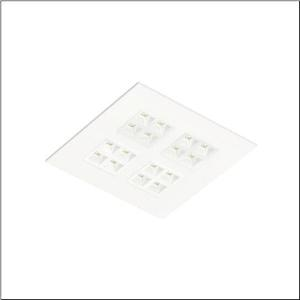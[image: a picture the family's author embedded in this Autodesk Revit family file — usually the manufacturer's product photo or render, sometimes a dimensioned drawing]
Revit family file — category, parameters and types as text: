
# Revit family: silica_31_square_51my6nms34wa
name_source: partatom
category: Lighting Fixtures
units: mm (PartAtom-declared; Revit-internal decimal feet)

## family parameters
Cut with Voids When Loaded = No
Host = Face
Light Source = No
Part Type = Normal
Room Calculation Point = No
Round Connector Dimension = Use Diameter
Shared = No

## types (1)
- --- (1 x LED, 6600 lm, 39 W, 3000K)
    Apparent Load = 39 VA
    CIE Flux Codes = 81 99 100 100 100
    Color Rendering = 80
    Color Temperature = 3000K
    Default Elevation = 1800 mm
    Description = Silica 31 Square, office luminaire, primary light control with lens, of PMMA, primary anti-glare with reflector, of PC, white, light emission: direct distribution, primary light characteristic: symmetric, installation type: lay-in mounting, LED, rated luminous flux: 4.580lm, luminous efficacy: 176lm/W, light colour: 830, colour temperature: 3000K, control gear: ON/OFF Multilumen, with terminal, 3-pole, mains connection: 220..240V, AC, 50/60Hz, rated input power: 26W, luminaire housing, of sheet steel, coated, traffic white (RAL 9016), module: M600, length: 595mm, width: 595mm, height: 43mm, protection rating (complete): IP20, insulation class (complete): insulation class II (safety insulation), certification: CE, impact resistance: IK03, permissible operating ambient temperature: -20..+35°C, standard: EN 50419, packaging unit: 1 piece
    Height = 0 mm  [stored 0 ft]
    Lamp = 1 x LED
    Lamp Light Flux = 6600 lm
    Lamp Power = 39 W
    Lamp count = 1
    Length = 595 mm
    Luminous efficacy = 169 lm/W
    Manufacturer = Siteco
    ModVariant = No
    Model = 51MY6NMS34WA
    Mounting Place = Ceiling
    Mounting Type = Recessed
    Number of Poles = 1
    OnlyDefault = Yes
    Power Factor = 1
    Product Name = Silica 31 Square
    Product group = office luminaire | ceiling recessed
    ProductGroupID = 400
    Protection Class = Protection class II
    Protection Degree = IP 20
    RLX_Detail_Level = 1
    RLX_Emergency_Light_Flux = 0 lm
    RLX_Emergency_Type = 0
    RLX_Emergency_Type_DB = No
    RlxData = <blob elided: 28813 chars, md5=8e445cca>
    Socket = socket
    Standby Power = 0 W
    System Light Flux = 6600 lm
    System Power = 39 W
    Type Comments = factory setting: luminous flux: 100 % | (ON | ON | ON | ON) | 1100 mA
    Type Image = l_1313651.jpg
    URL = http://relux.com
    VarID = @adj_044581
    Voltage = 0 V
    Weight = 0.00 kg
    Width = 595 mm

note: [stored X ft] marks values corroborated as IEEE doubles in the binary element streams (Revit-internal decimal feet)

## geometry (parser evidence)
native form markers: Blend x4, Sweep x9
no freeform markers — native parametric forms only
